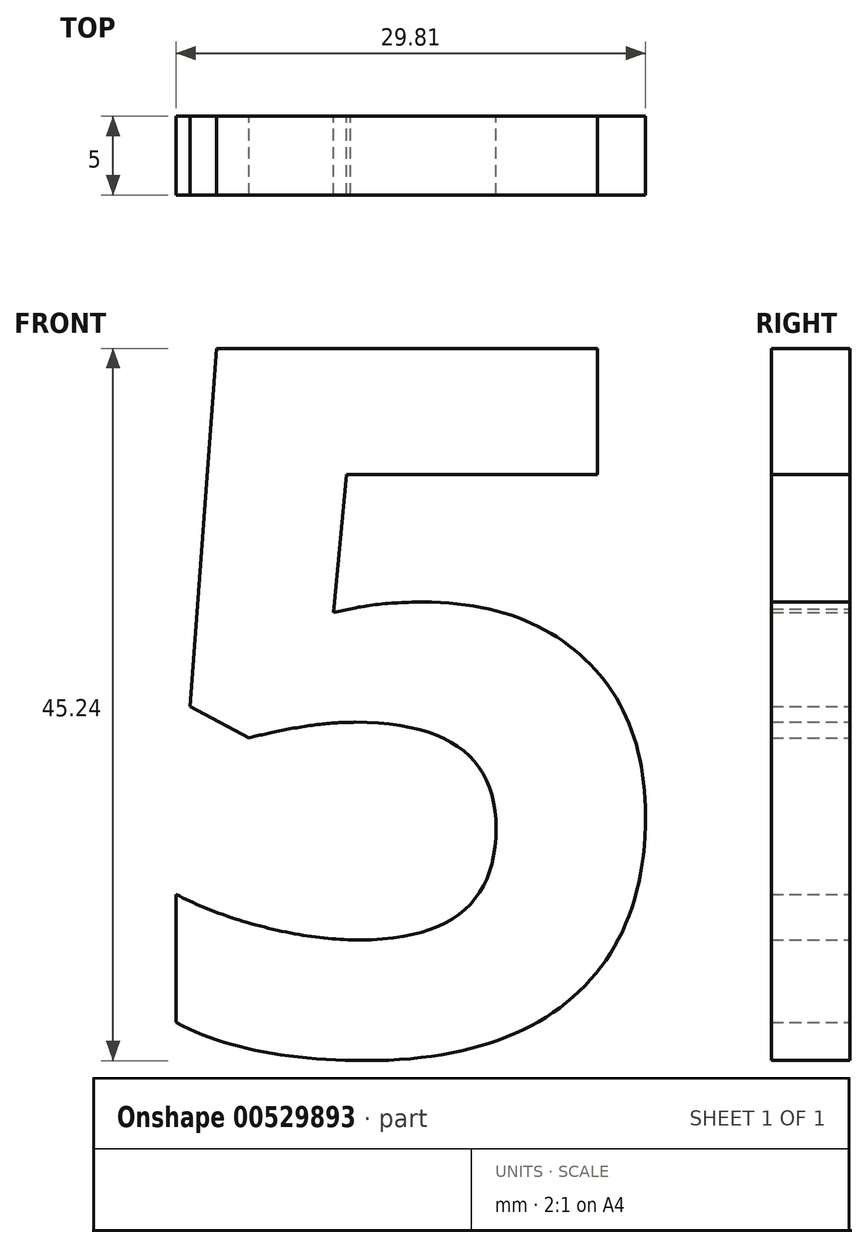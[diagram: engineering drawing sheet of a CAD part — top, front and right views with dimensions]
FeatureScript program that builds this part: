
annotation { "Feature Type Name" : "Feature", "Feature Type Description" : "" }
export const myFeature = defineFeature(function(context is Context, id is Id, definition is map)
    precondition{}
    {
        {
            var Q0;
            Q0=qCreatedBy(makeId("Front.planeOp"),FACE);
            var sketch = newSketch(context, id + "F0", { "sketchPlane" : qUnion([Q0])});
            skText(sketch, "E0", { "text": "5", "fontName": "OpenSans-Bold.ttf"});
            const initialGuessF0  = {"E0": [-0.06644, 0.02009, 1, 0, 0.045]};
            skSetInitialGuess(sketch, initialGuessF0);
            skSolve(sketch);
        }
        {
            var Q0;
            Q0=makeQuery(id+"F0.imprint","IMPRINT",FACE,{"disambiguationData":[TD([[makeQuery(id+"F0.imprint","IMPRINT",EDGE,{"derivedFrom":sQuery(id+"F0.wireOp",EDGE,"E0.sketch_text.stroke-0")}),-1.0]])]});
            extrude(context, id + "F1", {"entities" : qUnion([Q0]), "depth" : 5 * mm, "offsetDistance" : 25 * mm});
        }
    });
